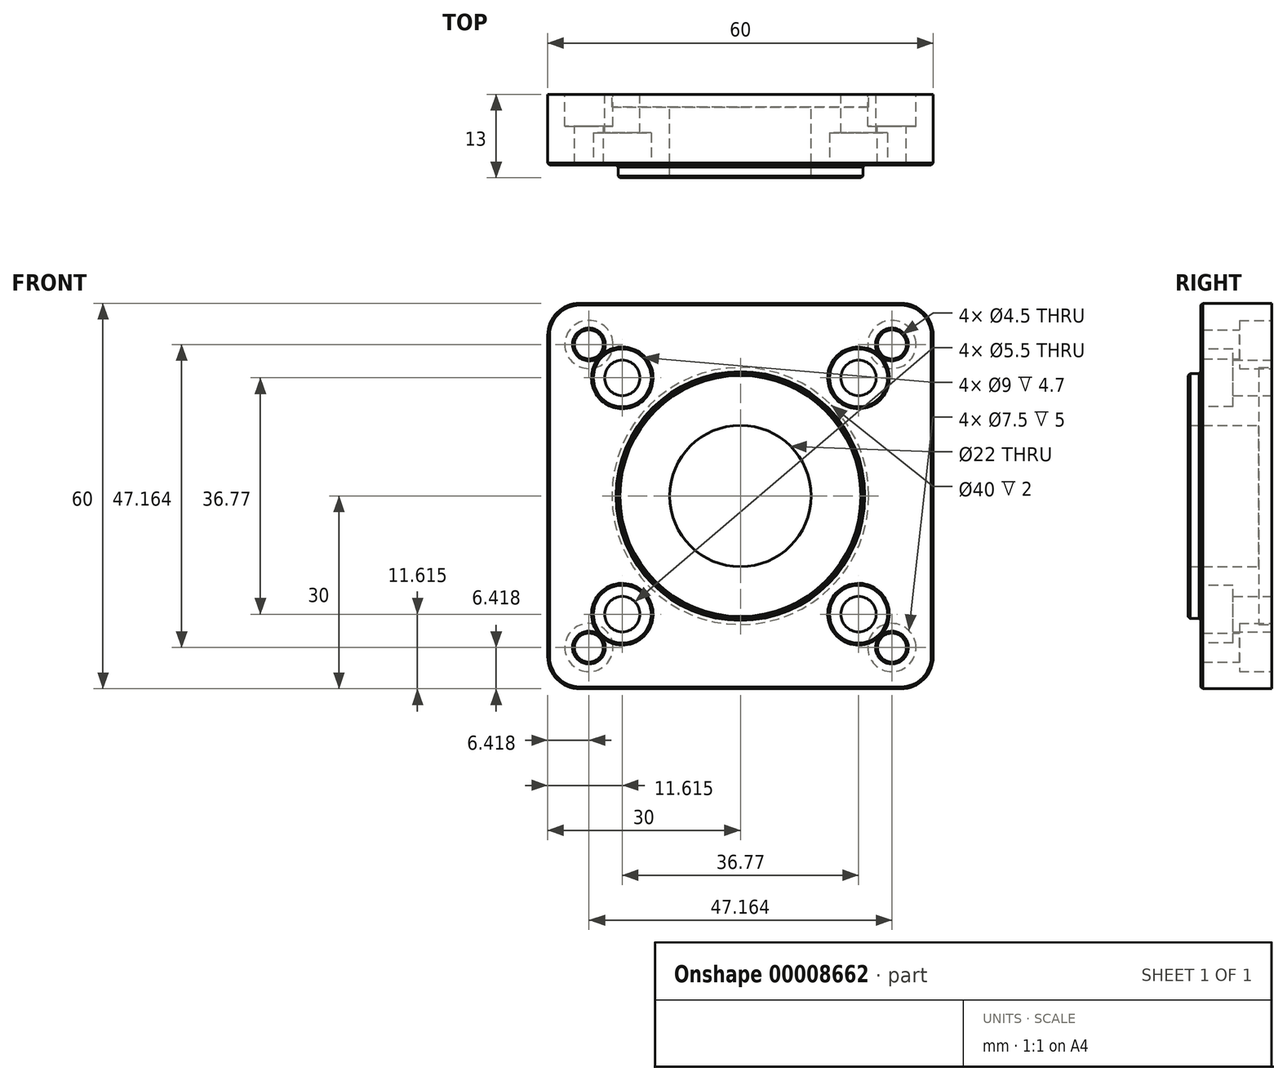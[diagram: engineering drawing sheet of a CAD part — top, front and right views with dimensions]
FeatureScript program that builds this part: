
annotation { "Feature Type Name" : "Feature", "Feature Type Description" : "" }
export const myFeature = defineFeature(function(context is Context, id is Id, definition is map)
    precondition{}
    {
        {
            var Q0;
            Q0=qCreatedBy(makeId("Front.planeOp"),FACE);
            var sketch = newSketch(context, id + "F0", { "sketchPlane" : qUnion([Q0])});
            skLineSegment(sketch, "E0.rect.bottom", {"start": v(-25, 30) * mm, "end": v(25, 30) * mm});
            skLineSegment(sketch, "E0.rect.top", {"start": v(-25, -30) * mm, "end": v(25, -30) * mm});
            skLineSegment(sketch, "E0.rect.left", {"start": v(-30, 25) * mm, "end": v(-30, -25) * mm});
            skLineSegment(sketch, "E0.rect.right", {"start": v(30, 25) * mm, "end": v(30, -25) * mm});
            skPoint(sketch, "E0.rect.middle", {"position": v(0, 0) * mm});
            skCircle(sketch, "E1", {"center": v(0, 0) * mm, "radius": 11 * mm});
            skCircle(sketch, "E2", {"center": v(-23.58, 23.58) * mm, "radius": 2.25 * mm});
            skCircle(sketch, "E3", {"center": v(-18.38, 18.38) * mm, "radius": 2.75 * mm});
            skCircle(sketch, "E4", {"center": v(18.38, 18.38) * mm, "radius": 2.75 * mm});
            skCircle(sketch, "E5", {"center": v(23.58, 23.58) * mm, "radius": 2.25 * mm});
            skCircle(sketch, "E6", {"center": v(18.38, -18.38) * mm, "radius": 2.75 * mm});
            skCircle(sketch, "E7", {"center": v(23.58, -23.58) * mm, "radius": 2.25 * mm});
            skCircle(sketch, "E8", {"center": v(-18.38, -18.38) * mm, "radius": 2.75 * mm});
            skCircle(sketch, "E9", {"center": v(-23.58, -23.58) * mm, "radius": 2.25 * mm});
            skPoint(sketch, "E10.visualSharp", {"position": v(-30, -30) * mm});
            skArc(sketch, "E10.filletArc", {"start": v(-30, -25) * mm, "mid": v(-28.54, -28.54) * mm, "end": v(-25, -30) * mm});
            skPoint(sketch, "E11.visualSharp", {"position": v(30, -30) * mm});
            skArc(sketch, "E11.filletArc", {"start": v(25, -30) * mm, "mid": v(28.54, -28.54) * mm, "end": v(30, -25) * mm});
            skPoint(sketch, "E12.visualSharp", {"position": v(30, 30) * mm});
            skArc(sketch, "E12.filletArc", {"start": v(30, 25) * mm, "mid": v(28.54, 28.54) * mm, "end": v(25, 30) * mm});
            skPoint(sketch, "E13.visualSharp", {"position": v(-30, 30) * mm});
            skArc(sketch, "E13.filletArc", {"start": v(-25, 30) * mm, "mid": v(-28.54, 28.54) * mm, "end": v(-30, 25) * mm});
            skSolve(sketch);
        }
        {
            var Q0;
            Q0=makeQuery(id+"F0.imprint","IMPRINT",FACE,{"disambiguationData":[TD([[makeQuery(id+"F0.imprint","IMPRINT",EDGE,{"derivedFrom":sQuery(id+"F0.wireOp",EDGE,"E0.rect.bottom")}),-1.0]])]});
            var Q1;
            Q1=makeQuery(id+"F0.imprint","IMPRINT",FACE,{"disambiguationData":[TD([[makeQuery(id+"F0.imprint","IMPRINT",EDGE,{"derivedFrom":sQuery(id+"F0.wireOp",EDGE,"E1")}),-1.0]])]});
            extrude(context, id + "F1", {"entities" : qUnion([Q0, Q1]), "depth" : 11 * mm});
        }
        {
            var Q0;
            Q0=makeQuery(id+"F1.opExtrude","CAP_FACE",FACE,{"disambiguationData":[OSD([sQuery(id+"F0.wireOp",EDGE,"E0.rect.bottom"),sQuery(id+"F0.wireOp",EDGE,"E0.rect.top"),sQuery(id+"F0.wireOp",EDGE,"E0.rect.left"),sQuery(id+"F0.wireOp",EDGE,"E0.rect.right"),sQuery(id+"F0.wireOp",EDGE,"E1")])],"isStart":false});
            var sketch = newSketch(context, id + "F2", { "sketchPlane" : qUnion([Q0])});
            skCircle(sketch, "E14", {"center": v(0, 0) * mm, "radius": 19.05 * mm});
            skSolve(sketch);
        }
        {
            var Q0;
            Q0=makeQuery(id+"F2.imprint","IMPRINT",FACE,{"disambiguationData":[TD([[makeQuery(id+"F2.imprint","IMPRINT",EDGE,{"derivedFrom":sQuery(id+"F2.wireOp",EDGE,"E14")}),1.0]])]});
            extrude(context, id + "F3", {"entities" : qUnion([Q0]), "operationType" : NewBodyOperationType.ADD, "depth" : 2 * mm});
        }
        {
            var Q0;
            Q0=makeQuery(id+"F1.opExtrude","CAP_FACE",FACE,{"disambiguationData":[OSD([sQuery(id+"F0.wireOp",EDGE,"E0.rect.bottom"),sQuery(id+"F0.wireOp",EDGE,"E0.rect.top"),sQuery(id+"F0.wireOp",EDGE,"E0.rect.left"),sQuery(id+"F0.wireOp",EDGE,"E0.rect.right"),sQuery(id+"F0.wireOp",EDGE,"E1"),sQuery(id+"F0.wireOp",EDGE,"E2"),sQuery(id+"F0.wireOp",EDGE,"E3"),sQuery(id+"F0.wireOp",EDGE,"E4"),sQuery(id+"F0.wireOp",EDGE,"E5"),sQuery(id+"F0.wireOp",EDGE,"E6"),sQuery(id+"F0.wireOp",EDGE,"E7"),sQuery(id+"F0.wireOp",EDGE,"E8"),sQuery(id+"F0.wireOp",EDGE,"E9")])],"isStart":false});
            var sketch = newSketch(context, id + "F4", { "sketchPlane" : qUnion([Q0])});
            skCircle(sketch, "E15", {"center": v(-18.38, 18.38) * mm, "radius": 4.5 * mm});
            skCircle(sketch, "E16", {"center": v(18.38, 18.38) * mm, "radius": 4.5 * mm});
            skCircle(sketch, "E17", {"center": v(18.38, -18.38) * mm, "radius": 4.5 * mm});
            skCircle(sketch, "E18", {"center": v(-18.38, -18.38) * mm, "radius": 4.5 * mm});
            skSolve(sketch);
        }
        {
            var Q0;
            Q0=makeQuery(id+"F4.imprint","IMPRINT",FACE,{"disambiguationData":[TD([[makeQuery(id+"F4.imprint","IMPRINT",EDGE,{"derivedFrom":sQuery(id+"F4.wireOp",EDGE,"E15")}),1.0]])]});
            var Q1;
            Q1=makeQuery(id+"F4.imprint","IMPRINT",FACE,{"disambiguationData":[TD([[makeQuery(id+"F4.imprint","IMPRINT",EDGE,{"derivedFrom":sQuery(id+"F4.wireOp",EDGE,"E18")}),1.0]])]});
            var Q2;
            Q2=makeQuery(id+"F4.imprint","IMPRINT",FACE,{"disambiguationData":[TD([[makeQuery(id+"F4.imprint","IMPRINT",EDGE,{"derivedFrom":sQuery(id+"F4.wireOp",EDGE,"E17")}),1.0]])]});
            var Q3;
            Q3=makeQuery(id+"F4.imprint","IMPRINT",FACE,{"disambiguationData":[TD([[makeQuery(id+"F4.imprint","IMPRINT",EDGE,{"derivedFrom":sQuery(id+"F4.wireOp",EDGE,"E16")}),1.0]])]});
            var Q4;
            Q4=sQuery(id+"F4.wireOp",EDGE,"E15");
            var Q5;
            Q5=sQuery(id+"F4.wireOp",EDGE,"E16");
            var Q6;
            Q6=sQuery(id+"F4.wireOp",EDGE,"E17");
            var Q7;
            Q7=sQuery(id+"F4.wireOp",EDGE,"E18");
            extrude(context, id + "F5", {"entities" : qUnion([Q0, Q1, Q2, Q3]), "operationType" : NewBodyOperationType.REMOVE, "surfaceEntities" : qUnion([Q4, Q5, Q6, Q7]), "oppositeDirection" : true, "depth" : 5 * mm});
        }
        {
            var Q0;
            Q0=makeQuery(id+"F1.opExtrude","CAP_FACE",FACE,{"disambiguationData":[OSD([sQuery(id+"F0.wireOp",EDGE,"E0.rect.bottom"),sQuery(id+"F0.wireOp",EDGE,"E0.rect.top"),sQuery(id+"F0.wireOp",EDGE,"E0.rect.left"),sQuery(id+"F0.wireOp",EDGE,"E0.rect.right"),sQuery(id+"F0.wireOp",EDGE,"E1"),sQuery(id+"F0.wireOp",EDGE,"E2"),sQuery(id+"F0.wireOp",EDGE,"E3"),sQuery(id+"F0.wireOp",EDGE,"E4"),sQuery(id+"F0.wireOp",EDGE,"E5"),sQuery(id+"F0.wireOp",EDGE,"E6"),sQuery(id+"F0.wireOp",EDGE,"E7"),sQuery(id+"F0.wireOp",EDGE,"E8"),sQuery(id+"F0.wireOp",EDGE,"E9")])],"isStart":true});
            var sketch = newSketch(context, id + "F6", { "sketchPlane" : qUnion([Q0])});
            skCircle(sketch, "E19", {"center": v(0, 0) * mm, "radius": 20 * mm});
            skSolve(sketch);
        }
        {
            var Q0;
            Q0=makeQuery(id+"F6.imprint","IMPRINT",FACE,{"disambiguationData":[TD([[makeQuery(id+"F6.imprint","IMPRINT",EDGE,{"derivedFrom":sQuery(id+"F6.wireOp",EDGE,"E19")}),1.0]])]});
            extrude(context, id + "F7", {"entities" : qUnion([Q0]), "operationType" : NewBodyOperationType.REMOVE, "oppositeDirection" : true, "depth" : 2 * mm});
        }
        {
            var Q0;
            Q0=makeQuery(id+"F1.opExtrude","CAP_FACE",FACE,{"disambiguationData":[OSD([sQuery(id+"F0.wireOp",EDGE,"E0.rect.bottom"),sQuery(id+"F0.wireOp",EDGE,"E0.rect.top"),sQuery(id+"F0.wireOp",EDGE,"E0.rect.left"),sQuery(id+"F0.wireOp",EDGE,"E0.rect.right"),sQuery(id+"F0.wireOp",EDGE,"E1"),sQuery(id+"F0.wireOp",EDGE,"E2"),sQuery(id+"F0.wireOp",EDGE,"E3"),sQuery(id+"F0.wireOp",EDGE,"E4"),sQuery(id+"F0.wireOp",EDGE,"E5"),sQuery(id+"F0.wireOp",EDGE,"E6"),sQuery(id+"F0.wireOp",EDGE,"E7"),sQuery(id+"F0.wireOp",EDGE,"E8"),sQuery(id+"F0.wireOp",EDGE,"E9")])],"isStart":true});
            var sketch = newSketch(context, id + "F8", { "sketchPlane" : qUnion([Q0])});
            skCircle(sketch, "E20", {"center": v(-23.58, 23.58) * mm, "radius": 3.75 * mm});
            skCircle(sketch, "E21", {"center": v(23.58, 23.58) * mm, "radius": 3.75 * mm});
            skCircle(sketch, "E22", {"center": v(23.58, -23.58) * mm, "radius": 3.75 * mm});
            skCircle(sketch, "E23", {"center": v(-23.58, -23.58) * mm, "radius": 3.75 * mm});
            skSolve(sketch);
        }
        {
            var Q0;
            Q0=makeQuery(id+"F8.imprint","IMPRINT",FACE,{"disambiguationData":[TD([[makeQuery(id+"F8.imprint","IMPRINT",EDGE,{"derivedFrom":sQuery(id+"F8.wireOp",EDGE,"E20")}),1.0]])]});
            var Q1;
            Q1=makeQuery(id+"F8.imprint","IMPRINT",FACE,{"disambiguationData":[TD([[makeQuery(id+"F8.imprint","IMPRINT",EDGE,{"derivedFrom":sQuery(id+"F8.wireOp",EDGE,"E21")}),1.0]])]});
            var Q2;
            Q2=makeQuery(id+"F8.imprint","IMPRINT",FACE,{"disambiguationData":[TD([[makeQuery(id+"F8.imprint","IMPRINT",EDGE,{"derivedFrom":sQuery(id+"F8.wireOp",EDGE,"E22")}),1.0]])]});
            var Q3;
            Q3=makeQuery(id+"F8.imprint","IMPRINT",FACE,{"disambiguationData":[TD([[makeQuery(id+"F8.imprint","IMPRINT",EDGE,{"derivedFrom":sQuery(id+"F8.wireOp",EDGE,"E23")}),1.0]])]});
            var Q4;
            Q4=sQuery(id+"F8.wireOp",EDGE,"E23");
            var Q5;
            Q5=sQuery(id+"F8.wireOp",EDGE,"E20");
            var Q6;
            Q6=sQuery(id+"F8.wireOp",EDGE,"E21");
            var Q7;
            Q7=sQuery(id+"F8.wireOp",EDGE,"E22");
            extrude(context, id + "F9", {"entities" : qUnion([Q0, Q1, Q2, Q3]), "operationType" : NewBodyOperationType.REMOVE, "surfaceEntities" : qUnion([Q4, Q5, Q6, Q7]), "oppositeDirection" : true, "depth" : 5 * mm});
        }
        {
            var Q0;
            Q0=makeQuery(id+"F3.opExtrude","CAP_EDGE",EDGE,{"disambiguationData":[OSD([sQuery(id+"F2.wireOp",EDGE,"E14")])],"isStart":false});
            var Q1;
            Q1=makeQuery(id+"F1.opExtrude","CAP_FACE",FACE,{"disambiguationData":[OSD([sQuery(id+"F0.wireOp",EDGE,"E0.rect.bottom"),sQuery(id+"F0.wireOp",EDGE,"E0.rect.top"),sQuery(id+"F0.wireOp",EDGE,"E0.rect.left"),sQuery(id+"F0.wireOp",EDGE,"E0.rect.right"),sQuery(id+"F0.wireOp",EDGE,"E1"),sQuery(id+"F0.wireOp",EDGE,"E2"),sQuery(id+"F0.wireOp",EDGE,"E3"),sQuery(id+"F0.wireOp",EDGE,"E4"),sQuery(id+"F0.wireOp",EDGE,"E5"),sQuery(id+"F0.wireOp",EDGE,"E6"),sQuery(id+"F0.wireOp",EDGE,"E7"),sQuery(id+"F0.wireOp",EDGE,"E8"),sQuery(id+"F0.wireOp",EDGE,"E9"),sQuery(id+"F0.wireOp",EDGE,"E10.filletArc"),sQuery(id+"F0.wireOp",EDGE,"E11.filletArc"),sQuery(id+"F0.wireOp",EDGE,"E12.filletArc"),sQuery(id+"F0.wireOp",EDGE,"E13.filletArc")])],"isStart":false});
            chamfer(context, id + "F10", {"entities" : qUnion([Q0, Q1]), "width" : .3 * mm, "tangentPropagation" : true});
        }
    });
